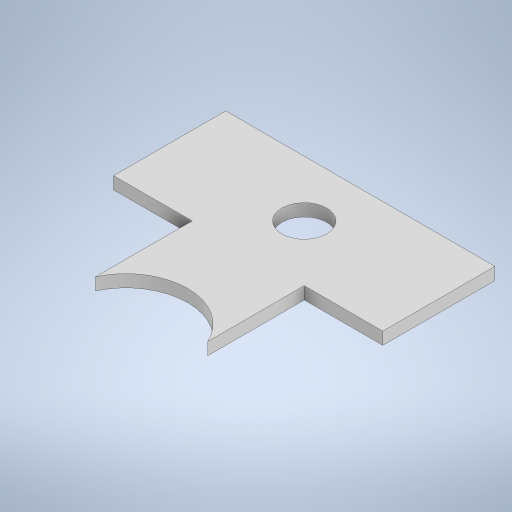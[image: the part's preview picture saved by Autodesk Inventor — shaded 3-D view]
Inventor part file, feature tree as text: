
AUTODESK INVENTOR PART (.ipt)
format: ipt  version: 2024.1 (Build 281209000, 209)  size: 248,832 bytes
history: native  units: mm
features: extrude x2, sketch x2, other x1, projected_geometry x1
ambient origin geometry x8: Origin, YZ Plane, XZ Plane, XY Plane, X Axis, Y Axis, Z Axis, Center Point
bodies: Body1 (feature_tree)
feature tree (6):
  other  "ソリッド1"
  extrude  "押し出し1"  Depth=114.0mm
  extrude  "押し出し2"  Depth=45.0mm
  sketch  "スケッチ1"
  sketch  "スケッチ2"
  projected_geometry  "投影ループ1"
